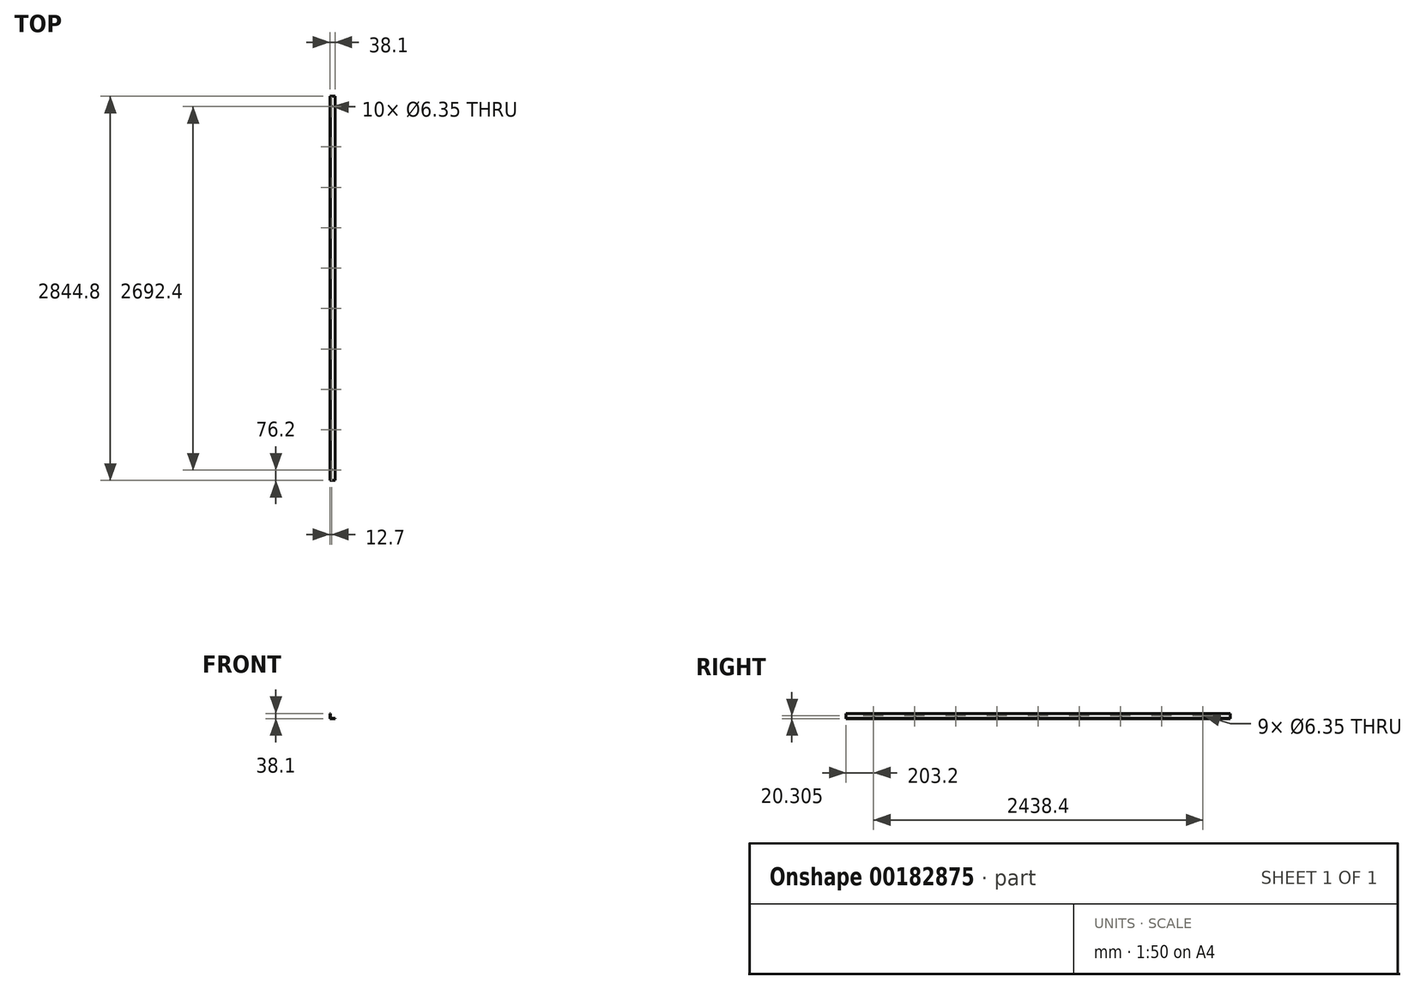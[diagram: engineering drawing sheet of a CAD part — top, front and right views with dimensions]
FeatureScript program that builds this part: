
annotation { "Feature Type Name" : "Feature", "Feature Type Description" : "" }
export const myFeature = defineFeature(function(context is Context, id is Id, definition is map)
    precondition{}
    {
        {
            var Q0;
            Q0=qCreatedBy(makeId("Front.planeOp"),FACE);
            var sketch = newSketch(context, id + "F0", { "sketchPlane" : qUnion([Q0])});
            skLineSegment(sketch, "E0.bottom", {"start": v(0, 0) * mm, "end": v(38.1, 0) * mm});
            skLineSegment(sketch, "E0.top", {"start": v(3.17, 3.17) * mm, "end": v(38.1, 3.17) * mm});
            skLineSegment(sketch, "E0.right", {"start": v(38.1, 0) * mm, "end": v(38.1, 3.17) * mm});
            skLineSegment(sketch, "E1.top", {"start": v(0, 38.1) * mm, "end": v(3.17, 38.1) * mm});
            skLineSegment(sketch, "E1.left", {"start": v(0, 0) * mm, "end": v(0, 38.1) * mm});
            skLineSegment(sketch, "E1.right", {"start": v(3.17, 3.17) * mm, "end": v(3.17, 38.1) * mm});
            skSolve(sketch);
        }
        {
            var Q0;
            Q0 = qSketchRegion(id + "F0", true);
            extrude(context, id + "F1", {"entities" : qUnion([Q0]), "oppositeDirection" : true, "depth" : 2844.8 * mm});
        }
        {
            var Q0;
            Q0=qCreatedBy(makeId("Top.planeOp"),FACE);
            var sketch = newSketch(context, id + "F2", { "sketchPlane" : qUnion([Q0])});
            skLineSegment(sketch, "E2", {"start": v(3.17, 76.2) * mm, "end": v(12.7, 76.2) * mm, "construction": true});
            skCircle(sketch, "E3", {"center": v(12.7, 76.2) * mm, "radius": 3.18 * mm});
            skCircle(sketch, "E4.0.1.0", {"center": v(12.7, 375.36) * mm, "radius": 3.18 * mm});
            skCircle(sketch, "E4.0.2.0", {"center": v(12.7, 674.51) * mm, "radius": 3.18 * mm});
            skCircle(sketch, "E4.0.3.0", {"center": v(12.7, 973.67) * mm, "radius": 3.18 * mm});
            skCircle(sketch, "E4.0.4.0", {"center": v(12.7, 1272.82) * mm, "radius": 3.18 * mm});
            skCircle(sketch, "E4.0.5.0", {"center": v(12.7, 1571.98) * mm, "radius": 3.18 * mm});
            skCircle(sketch, "E4.0.6.0", {"center": v(12.7, 1871.13) * mm, "radius": 3.18 * mm});
            skCircle(sketch, "E4.0.7.0", {"center": v(12.7, 2170.29) * mm, "radius": 3.18 * mm});
            skCircle(sketch, "E4.0.8.0", {"center": v(12.7, 2469.44) * mm, "radius": 3.18 * mm});
            skCircle(sketch, "E4.0.9.0", {"center": v(12.7, 2768.6) * mm, "radius": 3.18 * mm});
            skLineSegment(sketch, "E4.direction1", {"start": v(12.7, 76.2) * mm, "end": v(233.15, 76.2) * mm, "construction": true});
            skLineSegment(sketch, "E4.direction2", {"start": v(12.7, 76.2) * mm, "end": v(12.7, 375.36) * mm, "construction": true});
            skSolve(sketch);
        }
        {
            var Q0;
            Q0=qCreatedBy(makeId("Right.planeOp"),FACE);
            var sketch = newSketch(context, id + "F3", { "sketchPlane" : qUnion([Q0])});
            skCircle(sketch, "E5", {"center": v(203.2, 20.3) * mm, "radius": 3.18 * mm});
            skCircle(sketch, "E6.1.0.0", {"center": v(508, 20.3) * mm, "radius": 3.18 * mm});
            skCircle(sketch, "E6.2.0.0", {"center": v(812.8, 20.3) * mm, "radius": 3.18 * mm});
            skCircle(sketch, "E6.3.0.0", {"center": v(1117.6, 20.3) * mm, "radius": 3.18 * mm});
            skCircle(sketch, "E6.4.0.0", {"center": v(1422.4, 20.3) * mm, "radius": 3.18 * mm});
            skCircle(sketch, "E6.5.0.0", {"center": v(1727.2, 20.3) * mm, "radius": 3.18 * mm});
            skCircle(sketch, "E6.6.0.0", {"center": v(2032, 20.3) * mm, "radius": 3.18 * mm});
            skCircle(sketch, "E6.7.0.0", {"center": v(2336.8, 20.3) * mm, "radius": 3.18 * mm});
            skLineSegment(sketch, "E6.direction1", {"start": v(203.2, 20.3) * mm, "end": v(508, 20.3) * mm, "construction": true});
            skCircle(sketch, "E7.0.8.0", {"center": v(2641.6, 20.3) * mm, "radius": 3.18 * mm});
            skSolve(sketch);
        }
        {
            var Q0;
            Q0 = qSketchRegion(id + "F2", true);
            extrude(context, id + "F4", {"entities" : qUnion([Q0]), "operationType" : NewBodyOperationType.REMOVE, "depth" : 25.4 * mm});
        }
        {
            var Q0;
            Q0 = qSketchRegion(id + "F3", true);
            extrude(context, id + "F5", {"entities" : qUnion([Q0]), "operationType" : NewBodyOperationType.REMOVE, "depth" : 25.4 * mm});
        }
    });
